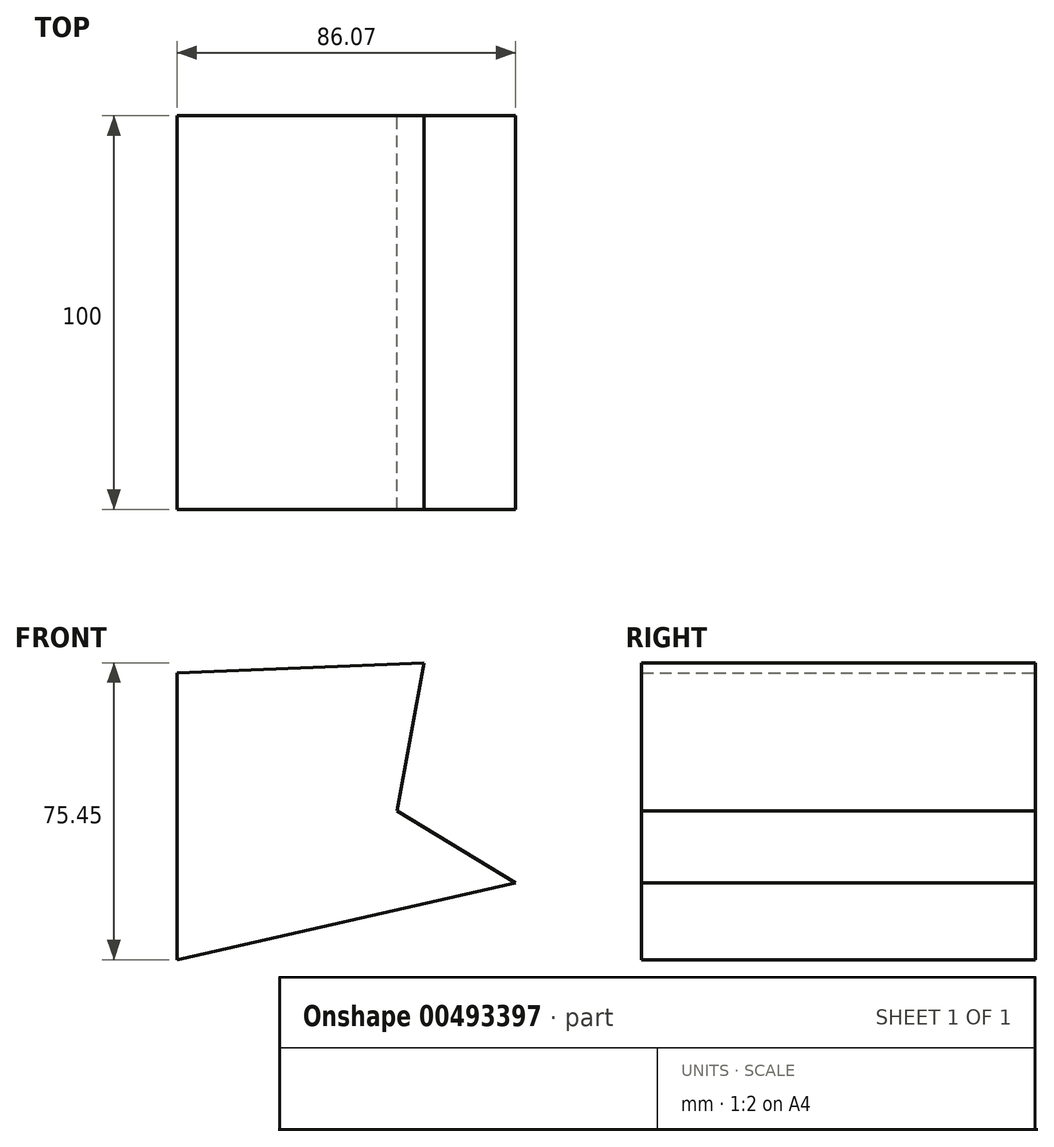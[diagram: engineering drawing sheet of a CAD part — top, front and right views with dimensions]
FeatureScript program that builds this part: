
annotation { "Feature Type Name" : "Feature", "Feature Type Description" : "" }
export const myFeature = defineFeature(function(context is Context, id is Id, definition is map)
    precondition{}
    {
        {
            var Q0;
            Q0=qCreatedBy(makeId("Front.planeOp"),FACE);
            var sketch = newSketch(context, id + "F0", { "sketchPlane" : qUnion([Q0])});
            skLineSegment(sketch, "E0", {"start": v(-37, 39.45) * mm, "end": v(-37, -33.42) * mm});
            skLineSegment(sketch, "E1", {"start": v(-37, -33.42) * mm, "end": v(49.06, -13.91) * mm});
            skLineSegment(sketch, "E2", {"start": v(49.06, -13.91) * mm, "end": v(18.93, 4.45) * mm});
            skLineSegment(sketch, "E3", {"start": v(18.93, 4.45) * mm, "end": v(25.82, 42.03) * mm});
            skLineSegment(sketch, "E4", {"start": v(25.82, 42.03) * mm, "end": v(-37, 39.45) * mm});
            skSolve(sketch);
        }
        {
            var Q0;
            Q0=makeQuery(id+"F0.imprint","IMPRINT",FACE,{"disambiguationData":[TD([[makeQuery(id+"F0.imprint","IMPRINT",EDGE,{"derivedFrom":sQuery(id+"F0.wireOp",EDGE,"E0")}),1.0]])]});
            extrude(context, id + "F1", {"entities" : qUnion([Q0]), "depth" : 100 * mm});
        }
    });
